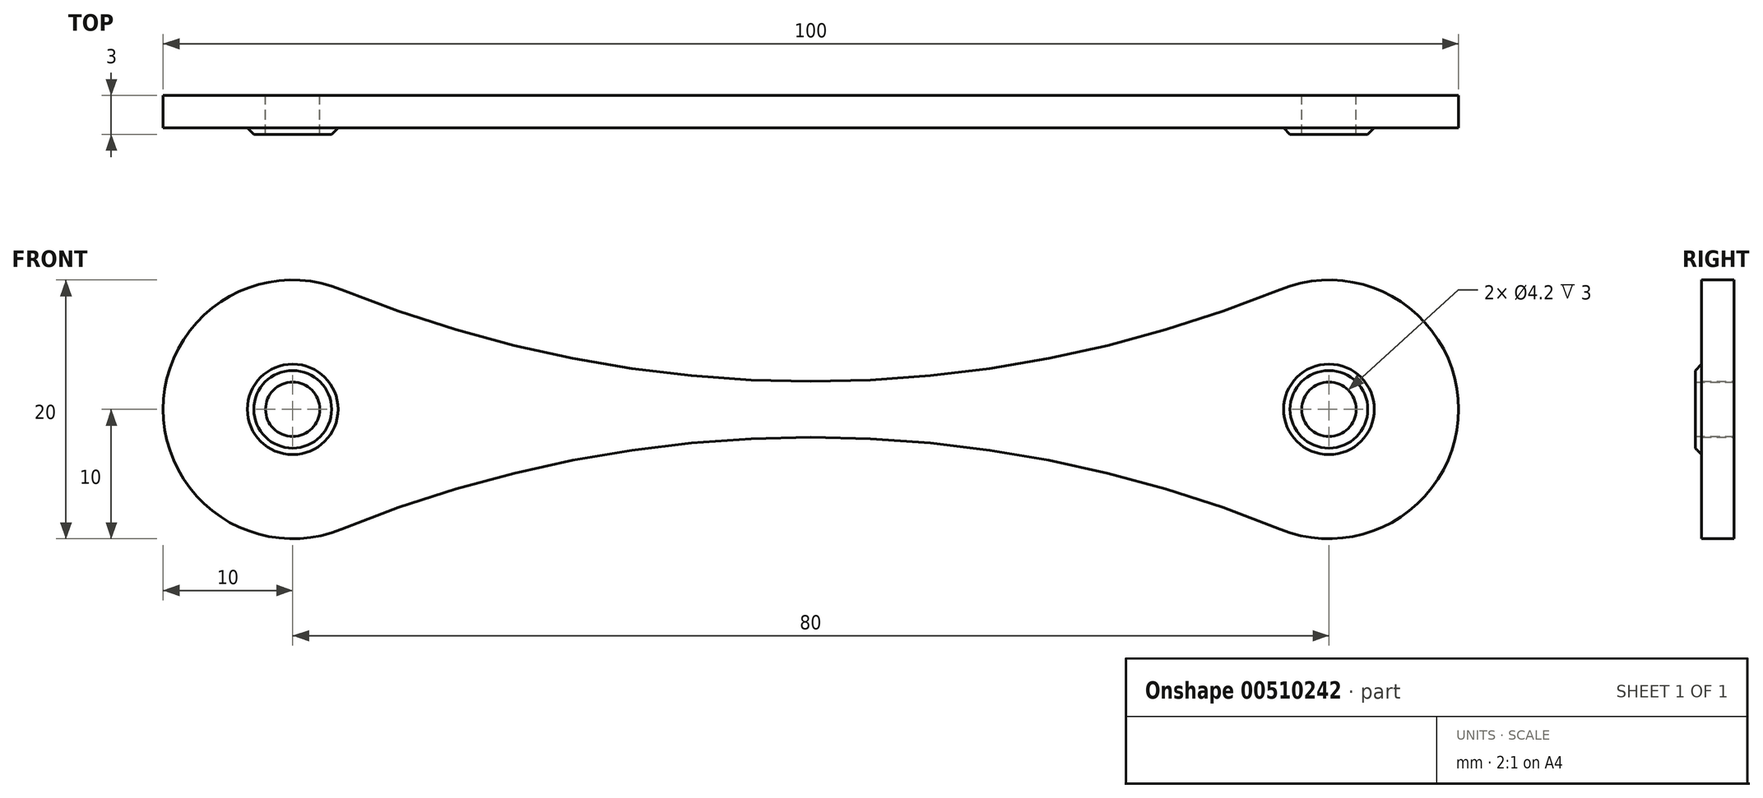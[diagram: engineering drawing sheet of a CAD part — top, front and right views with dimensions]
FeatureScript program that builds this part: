
annotation { "Feature Type Name" : "Feature", "Feature Type Description" : "" }
export const myFeature = defineFeature(function(context is Context, id is Id, definition is map)
    precondition{}
    {
        {
            var Q0;
            Q0=qCreatedBy(makeId("Front.planeOp"),FACE);
            var sketch = newSketch(context, id + "F0", { "sketchPlane" : qUnion([Q0])});
            skLineSegment(sketch, "E0.top", {"start": v(-50, -10) * mm, "end": v(50, -10) * mm});
            skLineSegment(sketch, "E0.left", {"start": v(-50, 16.21) * mm, "end": v(-50, -10) * mm});
            skLineSegment(sketch, "E0.right", {"start": v(50, 16.21) * mm, "end": v(50, -10) * mm});
            skCircle(sketch, "E1", {"center": v(0, 98.16) * mm, "radius": 100 * mm, "construction": true});
            skCircle(sketch, "E2", {"center": v(40, 0) * mm, "radius": 6 * mm});
            skCircle(sketch, "E3", {"center": v(-40, 0) * mm, "radius": 6 * mm});
            skCircle(sketch, "E4", {"center": v(0, 98.16) * mm, "radius": 96 * mm});
            skLineSegment(sketch, "E5", {"start": v(-40, 0) * mm, "end": v(40, 0) * mm, "construction": true});
            skSolve(sketch);
        }
        {
            var Q0;
            Q0=makeQuery(id+"F0.imprint","IMPRINT",FACE,{"disambiguationData":[TD([[makeQuery(id+"F0.imprint","IMPRINT",EDGE,{"derivedFrom":sQuery(id+"F0.wireOp",EDGE,"E0.top")}),1.0]])]});
            var Q1;
            Q1=makeQuery(id+"F0.imprint","IMPRINT",FACE,{"disambiguationData":[TD([[makeQuery(id+"F0.imprint","IMPRINT",EDGE,{"derivedFrom":sQuery(id+"F0.wireOp",EDGE,"E3")}),1.0]])]});
            var Q2;
            Q2=makeQuery(id+"F0.imprint","IMPRINT",FACE,{"disambiguationData":[TD([[makeQuery(id+"F0.imprint","IMPRINT",EDGE,{"derivedFrom":sQuery(id+"F0.wireOp",EDGE,"E2")}),1.0]])]});
            extrude(context, id + "F1", {"entities" : qUnion([Q0, Q1, Q2]), "depth" : 2.5 * mm, "offsetDistance" : 25 * mm});
        }
        {
            var Q0;
            Q0=makeQuery(id+"F0.imprint","IMPRINT",FACE,{"disambiguationData":[TD([[makeQuery(id+"F0.imprint","IMPRINT",EDGE,{"derivedFrom":sQuery(id+"F0.wireOp",EDGE,"E2")}),1.0]])]});
            var Q1;
            Q1=makeQuery(id+"F0.imprint","IMPRINT",FACE,{"disambiguationData":[TD([[makeQuery(id+"F0.imprint","IMPRINT",EDGE,{"derivedFrom":sQuery(id+"F0.wireOp",EDGE,"E3")}),1.0]])]});
            extrude(context, id + "F2", {"entities" : qUnion([Q0, Q1]), "operationType" : NewBodyOperationType.ADD, "depth" : 3 * mm, "offsetDistance" : 25 * mm, "hasDraft" : true, "draftAngle" : 45 * degree, "draftPullDirection" : true});
        }
        {
            var Q0;
            Q0=sQuery(id+"F0.wireOp",VERTEX,"E2.center");
            var Q1;
            Q1=sQuery(id+"F0.wireOp",VERTEX,"E3.center");
            var Q2;
            Q2=makeQuery(id+"F1.opExtrude","SWEPT_BODY",BODY,{"disambiguationData":[OSD([sQuery(id+"F0.wireOp",EDGE,"E0.top"),sQuery(id+"F0.wireOp",EDGE,"E0.left"),sQuery(id+"F0.wireOp",EDGE,"E0.right"),sQuery(id+"F0.wireOp",EDGE,"E4")])]});
            hole(context, id + "F3", {"style" : HoleStyle.SIMPLE, "endStyle" : HoleEndStyle.THROUGH, "oppositeDirection" : true, "standardTappedOrClearance" : lookupTablePath({ "standard" : "ISO", "fit" : "Close", "size" : "M4", "type" : "Clearance" }), "standardBlindInLast" : lookupTablePath({ "fit" : "Close", "standard" : "ISO", "size" : "M4", "type" : "Clearance" }), "holeDiameter" : 4.2 * mm, "majorDiameter" : 5 * mm, "isTappedThrough" : true, "tappedDepth" : 12 * mm, "tapClearance" : 3, "startFromSketch" : true, "locations" : qUnion([Q0, Q1]), "scope" : qUnion([Q2])});
        }
        {
            var Q0;
            Q0=makeQuery(id+"F1.opExtrude","SWEPT_EDGE",EDGE,{"disambiguationData":[OSD([sQuery(id+"F0.wireOp",EDGE,"E0.left"),sQuery(id+"F0.wireOp",EDGE,"E4")])]});
            var Q1;
            Q1=makeQuery(id+"F1.opExtrude","SWEPT_EDGE",EDGE,{"disambiguationData":[OSD([sQuery(id+"F0.wireOp",EDGE,"E0.right"),sQuery(id+"F0.wireOp",EDGE,"E4")])]});
            var Q2;
            Q2=makeQuery(id+"F1.opExtrude","SWEPT_EDGE",EDGE,{"disambiguationData":[OSD([sQuery(id+"F0.wireOp",EDGE,"E0.top"),sQuery(id+"F0.wireOp",EDGE,"E0.right")])]});
            var Q3;
            Q3=makeQuery(id+"F1.opExtrude","SWEPT_EDGE",EDGE,{"disambiguationData":[OSD([sQuery(id+"F0.wireOp",EDGE,"E0.top"),sQuery(id+"F0.wireOp",EDGE,"E0.left")])]});
            fillet(context, id + "F4", {"entities" : qUnion([Q0, Q1, Q2, Q3]), "radius" : 10 * mm, "tangentPropagation" : true, "allowEdgeOverflow" : false});
        }
        {
            var Q0;
            Q0=makeQuery(id+"F1.opExtrude","SWEPT_BODY",BODY,{"disambiguationData":[OSD([sQuery(id+"F0.wireOp",EDGE,"E0.top"),sQuery(id+"F0.wireOp",EDGE,"E0.left"),sQuery(id+"F0.wireOp",EDGE,"E0.right"),sQuery(id+"F0.wireOp",EDGE,"E4")])]});
            var Q1;
            Q1=qCreatedBy(makeId("Top.planeOp"),FACE);
            mirror(context, id + "F5", {"entities" : qUnion([Q0]), "mirrorPlane" : qUnion([Q1])});
        }
        {
            var Q0;
            Q0=makeQuery(id+"F1.opExtrude","SWEPT_BODY",BODY,{"disambiguationData":[OSD([sQuery(id+"F0.wireOp",EDGE,"E0.top"),sQuery(id+"F0.wireOp",EDGE,"E0.left"),sQuery(id+"F0.wireOp",EDGE,"E0.right"),sQuery(id+"F0.wireOp",EDGE,"E4")])]});
            var Q1;
            Q1=makeQuery(id+"F5.opPattern","COPY",BODY,{"derivedFrom":makeQuery(id+"F1.opExtrude","SWEPT_BODY",BODY,{"disambiguationData":[OSD([sQuery(id+"F0.wireOp",EDGE,"E0.top"),sQuery(id+"F0.wireOp",EDGE,"E0.left"),sQuery(id+"F0.wireOp",EDGE,"E0.right"),sQuery(id+"F0.wireOp",EDGE,"E4")])]}),"instanceName":"1"});
            booleanBodies(context, id + "F6", {"operationType" : BooleanOperationType.INTERSECTION, "tools" : qUnion([Q0, Q1])});
        }
    });
